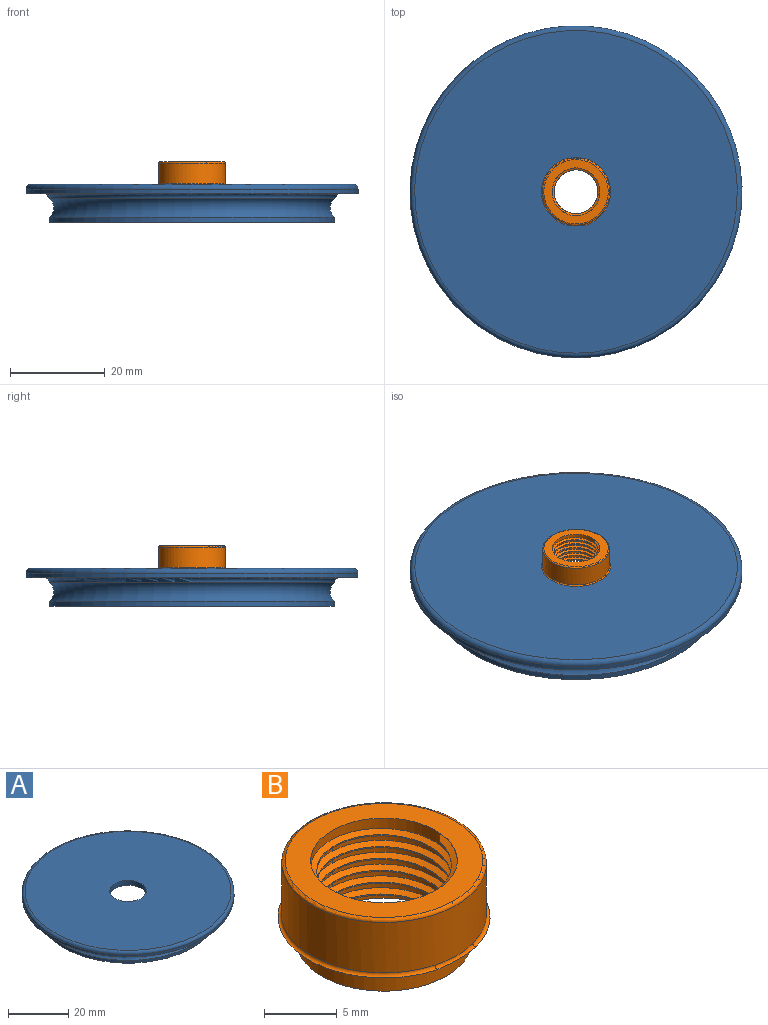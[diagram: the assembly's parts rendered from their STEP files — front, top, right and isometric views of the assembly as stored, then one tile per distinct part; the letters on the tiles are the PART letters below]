
ASSEMBLY  parts=2 mates=1
PART A: 13 faces, bbox 76x76x8 mm
  f0: plane 53.4x53.4mm, normal (0,0,-1), area 2124.6mm2, adj f9,f10
  f1: cylinder r=27.7mm len=55.4mm, axis (0,0,-1), area 870.2mm2, adj f2,f10
  f2: plane 60.19x60.19mm, normal (0,0,-1), area 434.5mm2, adj f1,f3
  f3: cylinder r=30.09mm len=60.19mm, axis (0,0,-1), area 205.1mm2, adj f2,f4
  f4: torus R=31.7mm, axis (0,0,-1), area 808.9mm2, adj f3,f5
  f5: cylinder r=30.09mm len=60.19mm, axis (0,0,-1), area 16.1mm2, adj f4,f11
  f6: plane 70.19x70.19mm, normal (0,0,-1), area 831.7mm2, adj f7,f11
  f7: cylinder r=35.09mm len=70.19mm, axis (0,0,-1), area 220.5mm2, adj f6,f12
  f8: plane 68.19x68.19mm, normal (0,0,1), area 3536.6mm2, adj f9,f12
  f9: cylinder r=6.05mm len=12.1mm, axis (0,0,-1), area 76mm2, adj f0,f8
  f10: torus R=26.7mm, axis (0,0,1), area 269.8mm2, adj f0,f1
  f11: torus R=31.09mm, axis (0,0,1), area 300.6mm2, adj f5,f6
  f12: torus R=34.09mm, axis (0,0,-1), area 342.8mm2, adj f7,f8
PART B: 21 faces, bbox 16.4x15.8x7.3 mm
  f0: cylinder r=6.05mm len=12.1mm, axis (0,0,1), area 76mm2, adj f5,f20
  f1: plane 0.6x0.49mm, normal (-0.64,0.77,0), area 0.2mm2, adj f2,f3,f4,f6
  f2: bspline ~11.66x10.1mm, area 91.1mm2, adj f1,f3,f5,f6,f7,f8,f9,f10
  f3: cylinder r=4.64mm len=9.27mm, axis (0,0,-1), area 28.6mm2, adj f1,f2,f4,f5
  f4: bspline ~11.66x10.1mm, area 96.5mm2, adj f1,f3,f5,f6,f7,f8,f9,f10
  f5: plane 12.31x12.31mm, normal (0,0,-1), area 39.2mm2, adj f0,f2,f3,f4,f12
  f6: cylinder r=5.05mm len=10.1mm, axis (0,0,-1), area 26.2mm2, adj f1,f2,f4,f7,f13
  f7: cylinder r=5.05mm len=10.1mm, axis (0,0,-1), area 13.4mm2, adj f2,f4,f6,f8
  f8: cylinder r=5.05mm len=10.1mm, axis (0,0,-1), area 13.4mm2, adj f2,f4,f7,f9
  f9: cylinder r=5.05mm len=10.1mm, axis (0,0,-1), area 13.4mm2, adj f2,f4,f8,f10
  f10: cylinder r=5.05mm len=10.1mm, axis (0,0,-1), area 13.4mm2, adj f2,f4,f9,f11
  f11: cylinder r=5.05mm len=10.1mm, axis (0,0,-1), area 13.4mm2, adj f2,f4,f10,f12
  f12: cylinder r=5.05mm len=9.52mm, axis (0,0,-1), area 2.8mm2, adj f2,f5,f11
  f13: plane 13.6x13.6mm, normal (0,0,1), area 65.1mm2, adj f6,f19
  f14: cylinder r=7.05mm len=14.1mm, axis (0,0,-1), area 188.3mm2, adj f15,f16,f17,f18,f19
  f15: bspline ~4.77x0.59mm, area 1.3mm2, adj f14,f16,f17,f20
  f16: torus R=7.3mm, axis (0,0,1), area 7.3mm2, adj f14,f15,f18,f20
  f17: torus R=7.3mm, axis (0,0,1), area 7.3mm2, adj f14,f15,f18,f20
  f18: bspline ~4.77x0.59mm, area 1.3mm2, adj f14,f16,f17,f20
  f19: torus R=6.8mm, axis (0,0,1), area 17.2mm2, adj f13,f14
  f20: plane 14.73x14.51mm, normal (0,0,-1), area 51.9mm2, adj f0,f15,f16,f17,f18
PLACE A rot(axis=(0,0,1),90deg) t=(0,0,0)mm
PLACE B t=(0,0,-2)mm
MATE fastened B.f14 <-> A.f1  axis (0,0,-1) through (0,0,0)mm
